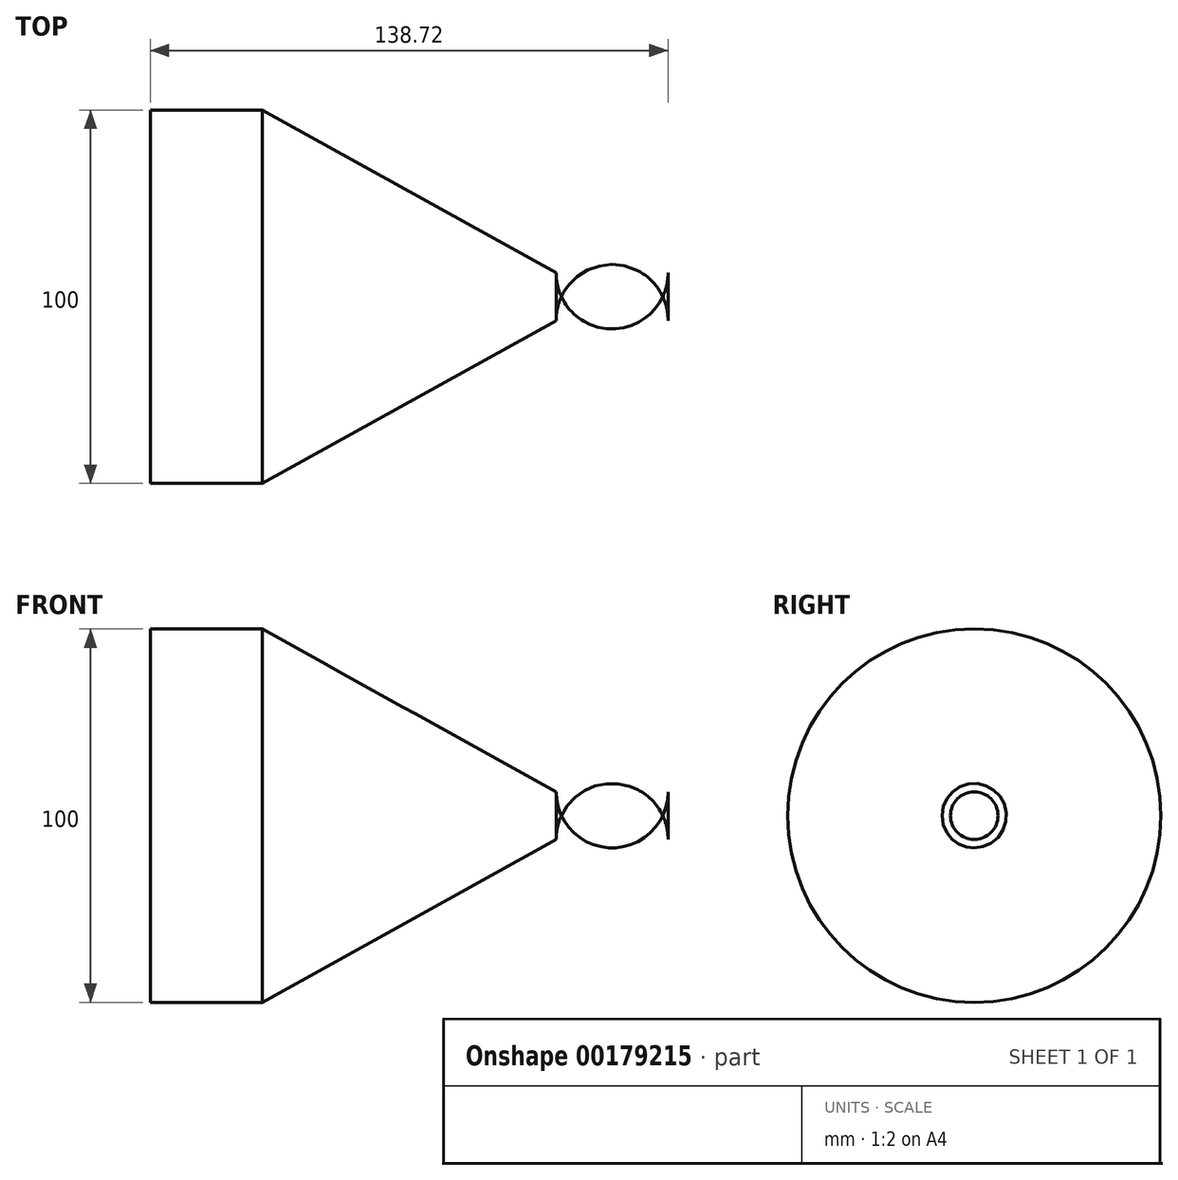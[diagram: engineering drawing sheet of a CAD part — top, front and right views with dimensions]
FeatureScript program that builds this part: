
annotation { "Feature Type Name" : "Feature", "Feature Type Description" : "" }
export const myFeature = defineFeature(function(context is Context, id is Id, definition is map)
    precondition{}
    {
        {
            var Q0;
            Q0=qCreatedBy(makeId("Front.planeOp"),FACE);
            var sketch = newSketch(context, id + "F0", { "sketchPlane" : qUnion([Q0])});
            skLineSegment(sketch, "E0", {"start": v(0, 0) * mm, "end": v(150, 0) * mm, "construction": true});
            skLineSegment(sketch, "E1", {"start": v(0, 0) * mm, "end": v(0, 50) * mm});
            skLineSegment(sketch, "E2", {"start": v(0, 50) * mm, "end": v(30, 50) * mm});
            skLineSegment(sketch, "E3", {"start": v(30, 50) * mm, "end": v(108.72, 6.37) * mm});
            skLineSegment(sketch, "E4", {"start": v(108.72, 6.37) * mm, "end": v(138.72, 6.37) * mm, "construction": true});
            skArc(sketch, "E5", {"start": v(138.72, 6.37) * mm, "mid": v(123.72, 21.37) * mm, "end": v(108.72, 6.37) * mm});
            skLineSegment(sketch, "E6", {"start": v(138.72, 6.37) * mm, "end": v(138.72, 0) * mm});
            skLineSegment(sketch, "E7", {"start": v(138.72, 0) * mm, "end": v(0, 0) * mm});
            skSolve(sketch);
        }
        {
            var Q0;
            Q0=makeQuery(id+"F0.imprint","IMPRINT",FACE,{"disambiguationData":[TD([[makeQuery(id+"F0.imprint","IMPRINT",EDGE,{"derivedFrom":sQuery(id+"F0.wireOp",EDGE,"E1")}),-1.0]])]});
            var Q1;
            Q1=sQuery(id+"F0.wireOp",EDGE,"E0");
            revolve(context, id + "F1", {"entities" : qUnion([Q0]), "axis" : qUnion([Q1]), "revolveType" : RevolveType.FULL});
        }
    });
